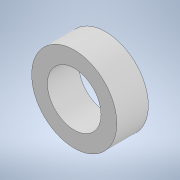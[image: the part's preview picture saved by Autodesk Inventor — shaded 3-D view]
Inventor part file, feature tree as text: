
AUTODESK INVENTOR PART (.ipt)
format: ipt  version: 2022 (Build 260153000, 153)  size: 98,816 bytes
history: native  units: mm
features: extrude x1, sketch x1
ambient origin geometry x8: Origin, YZ Plane, XZ Plane, XY Plane, X Axis, Y Axis, Z Axis, Center Point
bodies: Solid1 (feature_tree)
feature tree (2):
  extrude  "Extrusion1"  Depth=3.0mm
  sketch  "Sketch1"  dims[d0=5.1mm d1=1.5mm d2=3.0mm d3=0.0mm]
